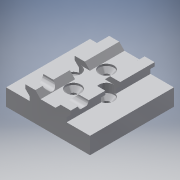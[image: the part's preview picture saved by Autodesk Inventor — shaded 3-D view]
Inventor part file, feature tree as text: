
AUTODESK INVENTOR PART (.ipt)
format: ipt  version: 2019 (Build 230136000, 136)  size: 259,584 bytes
history: native  units: in
note: dims shown in document units (in); Inventor stores cm internally (conversion verified against a paired STEP export)
features: extrude x7, sketch x4, other x3, chamfer x2, mirror x1, hole x1, projected_geometry x1, reference x1
ambient origin geometry x8: Origin, YZ Plane, XZ Plane, XY Plane, X Axis, Y Axis, Z Axis, Center Point
bodies: Solid1 (feature_tree)
feature tree (20):
  extrude  "Extrusion1"  Depth=2.0in
  extrude  "Extrusion2"  Depth=0.1in
  mirror  "Mirror1"
  hole  "Hole1"  [1 undecoded]
  sketch  "Sketch4"  dims[d7=0.125in d8=0.25in d9=0.55in d10=0.45in d11=0.4in d12=0.0in d13=0.7874in d14=0.1654in d15=0.75in d16=0.375in d17=0.25in d18=0.5635in d19=0.5in d20=0.8108in d21=0.3543in d22=0.4in d23=0.0in d24=0.2126in d25=0.0in d26=0.0078in d27=0.0078in d28=0.0078in d29=0.0078in d30=0.0078in d31=0.0078in d32=0.2in d33=0.0in d34=0.0945in d35=0.125in d36=45.0deg d37=0.045in d38=0.0in d39=0.0945in d40=0.125in d41=45.0deg d42=0.0145in d43=0.0in d44=0.3in d45=0.257in]
  extrude  "Extrusion3"  Depth=0.125in
  extrude  "Extrusion4"  Depth=0.125in
  extrude  "Extrusion5"  Depth=0.125in
  chamfer  "Chamfer1"  Distance=0.4in
  extrude  "Extrusion6"  Depth=0.125in
  chamfer  "Chamfer2"  Distance=0.3543in
  extrude  "Extrusion7"  Depth=0.4in TaperAngle=0.0deg
  sketch  "Sketch1"  dims[d0=2.0in d1=2.0in]
  sketch  "Sketch2"  dims[d2=0.4in d3=0.0in d4=0.1in]
  sketch  "Sketch3"  dims[d5=0.1in d6=135.0deg]
  projected_geometry  "Projected Loop1"
  reference  "Reference2"
  parser-record x1  (decoder bookkeeping rows leaked as tree rows — omitted from the tree; the rows remain in map.json)
  other  "Tool_Head_Assem.iam"
  other  "Gantry_Mount:1"
note: 1 required parameter value undecoded (feature->parameter linkage not recoverable at this tier; creation-order binding heuristic only, values carry confidence <= 0.55)
note: 1 file-system path scrubbed to <path> (originals preserved in map.json)
